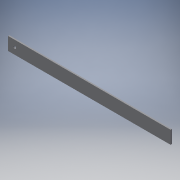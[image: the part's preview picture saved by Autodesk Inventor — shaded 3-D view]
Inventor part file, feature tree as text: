
AUTODESK INVENTOR PART (.ipt)
format: ipt  version: 2018 (Build 220112000, 112)  size: 111,104 bytes
history: native  units: in
note: dims shown in document units (in); Inventor stores cm internally (conversion verified against a paired STEP export)
features: extrude x3, sketch x3
ambient origin geometry x8: Origin, YZ Plane, XZ Plane, XY Plane, X Axis, Y Axis, Z Axis, Center Point
bodies: Solid1 (feature_tree)
feature tree (6):
  extrude  "Extrusion1"  Depth=1.0in
  extrude  "Extrusion2"  Depth=0.1in
  extrude  "Extrusion3"  Depth=1.0in
  sketch  "Sketch1"  dims[d2=12.5in d3=1.0in]
  sketch  "Sketch2"  dims[d4=0.1in d5=0.0in d6=0.2031in]
  sketch  "Sketch3"  dims[d7=0.5in d8=0.5in d9=1.0in d10=0.0in d11=0.2031in d12=0.5in d13=0.5in d14=1.0in d15=0.0in]
